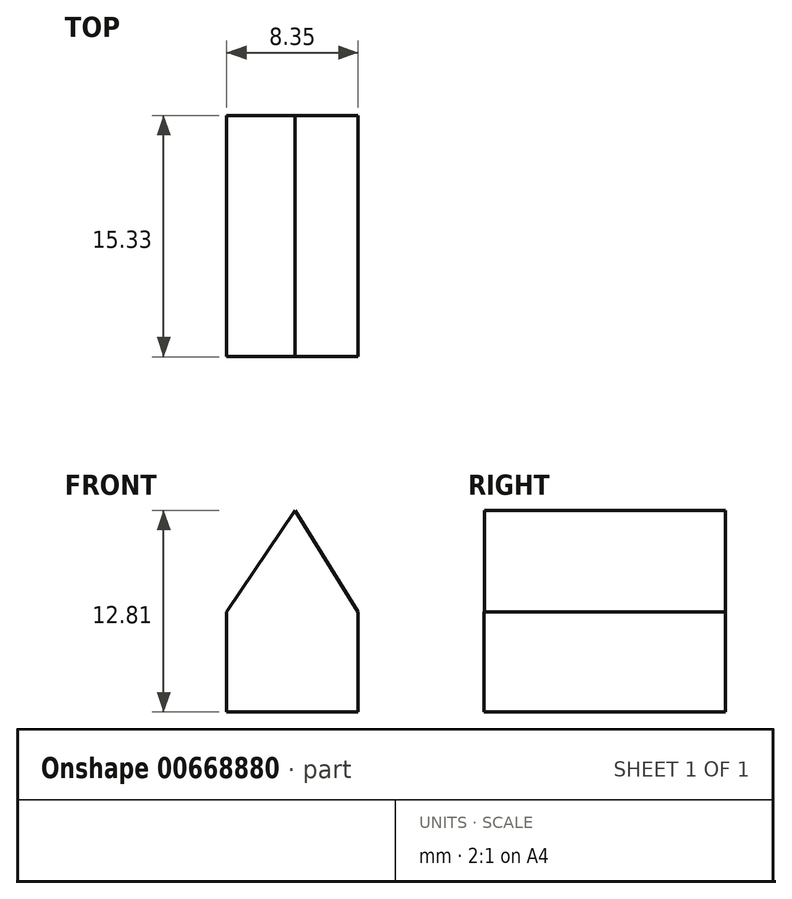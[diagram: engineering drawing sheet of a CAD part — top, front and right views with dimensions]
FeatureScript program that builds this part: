
annotation { "Feature Type Name" : "Feature", "Feature Type Description" : "" }
export const myFeature = defineFeature(function(context is Context, id is Id, definition is map)
    precondition{}
    {
        {
            var Q0;
            Q0=qCreatedBy(makeId("Top.planeOp"),FACE);
            var sketch = newSketch(context, id + "F0", { "sketchPlane" : qUnion([Q0])});
            skLineSegment(sketch, "E0.bottom", {"start": v(-4.34, 7.73) * mm, "end": v(4, 7.73) * mm});
            skLineSegment(sketch, "E0.top", {"start": v(-4.34, -7.6) * mm, "end": v(4, -7.6) * mm});
            skLineSegment(sketch, "E0.left", {"start": v(-4.34, 7.73) * mm, "end": v(-4.34, -7.6) * mm});
            skLineSegment(sketch, "E0.right", {"start": v(4, 7.73) * mm, "end": v(4, -7.6) * mm});
            skSolve(sketch);
        }
        {
            var Q0;
            Q0 = qSketchRegion(id + "F0", true);
            extrude(context, id + "F1", {"entities" : qUnion([Q0]), "depth" : 6.35 * mm, "offsetDistance" : 25.4 * mm});
        }
        {
            var Q0;
            Q0=makeQuery(id+"F1.opExtrude","SWEPT_FACE",FACE,{"disambiguationData":[OSD([sQuery(id+"F0.wireOp",EDGE,"E0.bottom")])]});
            var sketch = newSketch(context, id + "F2", { "sketchPlane" : qUnion([Q0])});
            skLineSegment(sketch, "E1", {"start": v(-4, 6.35) * mm, "end": v(4.34, 6.35) * mm});
            skLineSegment(sketch, "E2", {"start": v(4.34, 6.35) * mm, "end": v(0, 12.8) * mm});
            skLineSegment(sketch, "E3", {"start": v(0, 12.8) * mm, "end": v(-4, 6.35) * mm});
            skSolve(sketch);
        }
        {
            var Q0;
            Q0 = qSketchRegion(id + "F2", true);
            extrude(context, id + "F3", {"entities" : qUnion([Q0]), "operationType" : NewBodyOperationType.ADD, "oppositeDirection" : true, "depth" : 15.32 * mm, "offsetDistance" : 25.4 * mm});
        }
    });
